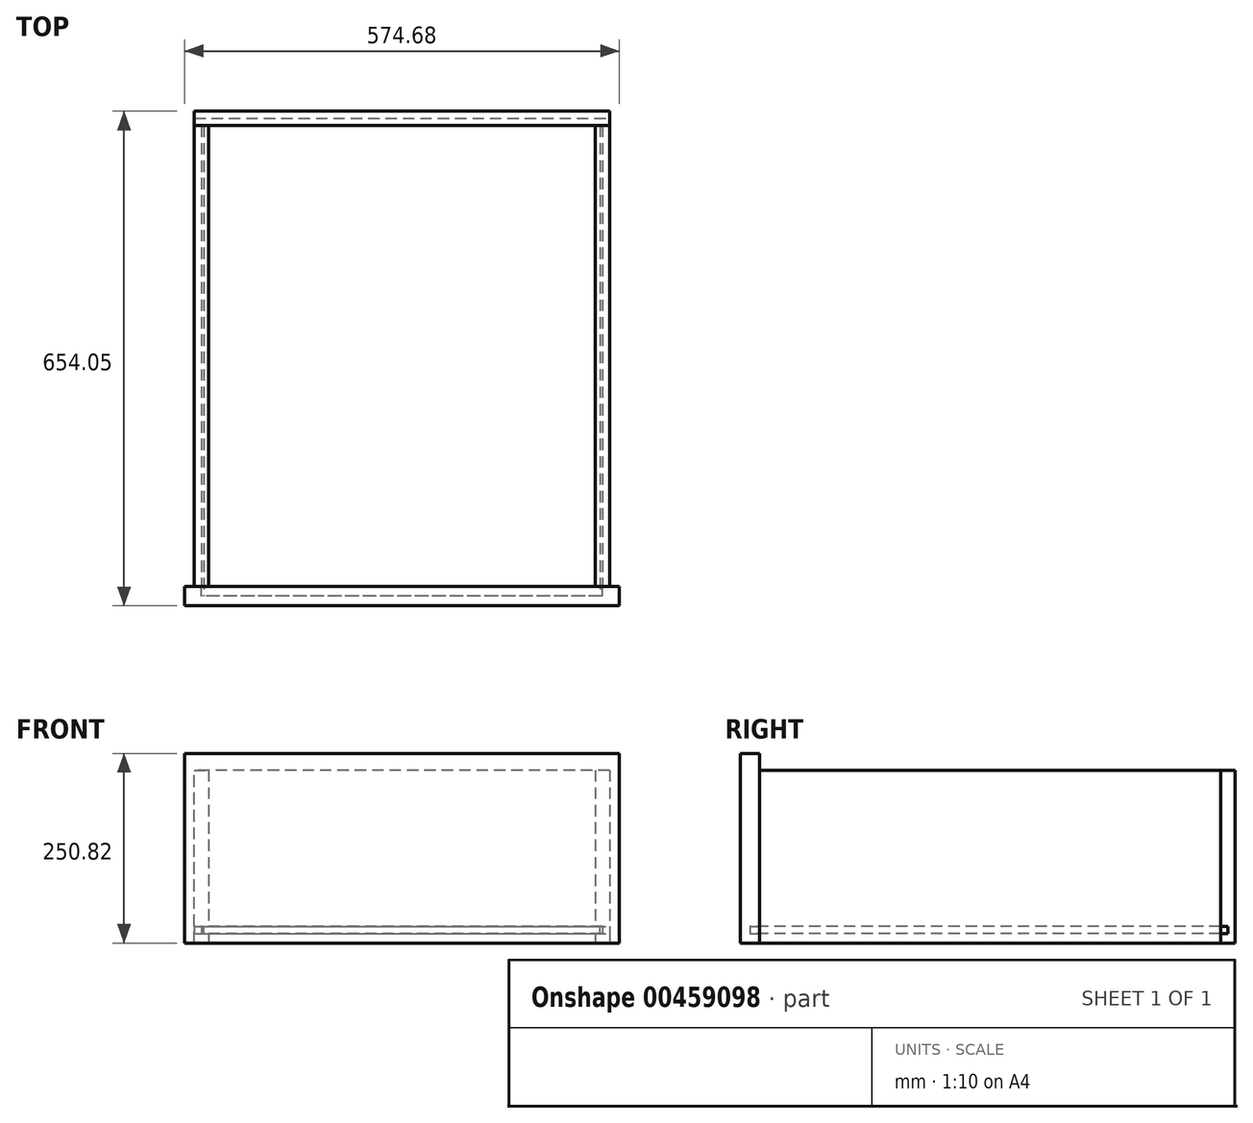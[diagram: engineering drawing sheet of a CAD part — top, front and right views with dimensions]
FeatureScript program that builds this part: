
annotation { "Feature Type Name" : "Feature", "Feature Type Description" : "" }
export const myFeature = defineFeature(function(context is Context, id is Id, definition is map)
    precondition{}
    {
        {
            var Q0;
            Q0=qCreatedBy(makeId("Front.planeOp"),FACE);
            var sketch = newSketch(context, id + "F0", { "sketchPlane" : qUnion([Q0])});
            skLineSegment(sketch, "E0.bottom", {"start": v(-287.34, 125.41) * mm, "end": v(287.34, 125.41) * mm});
            skLineSegment(sketch, "E0.top", {"start": v(-287.34, -125.41) * mm, "end": v(287.34, -125.41) * mm});
            skLineSegment(sketch, "E0.left", {"start": v(-287.34, 125.41) * mm, "end": v(-287.34, -125.41) * mm});
            skLineSegment(sketch, "E0.right", {"start": v(287.34, 125.41) * mm, "end": v(287.34, -125.41) * mm});
            skSolve(sketch);
        }
        {
            var Q0;
            Q0=makeQuery(id+"F0.imprint","IMPRINT",FACE,{"disambiguationData":[TD([[makeQuery(id+"F0.imprint","IMPRINT",EDGE,{"derivedFrom":sQuery(id+"F0.wireOp",EDGE,"E0.bottom")}),-1.0]])]});
            extrude(context, id + "F1", {"entities" : qUnion([Q0]), "depth" : 25.4 * mm});
        }
        {
            var Q0;
            Q0=makeQuery(id+"F1.opExtrude","CAP_FACE",FACE,{"disambiguationData":[OSD([sQuery(id+"F0.wireOp",EDGE,"E0.bottom"),sQuery(id+"F0.wireOp",EDGE,"E0.top"),sQuery(id+"F0.wireOp",EDGE,"E0.left"),sQuery(id+"F0.wireOp",EDGE,"E0.right")])],"isStart":true});
            var sketch = newSketch(context, id + "F2", { "sketchPlane" : qUnion([Q0])});
            skLineSegment(sketch, "E1.bottom", {"start": v(-274.64, 103.19) * mm, "end": v(-255.59, 103.19) * mm});
            skLineSegment(sketch, "E1.top", {"start": v(-274.64, -125.41) * mm, "end": v(-255.59, -125.41) * mm});
            skLineSegment(sketch, "E1.right", {"start": v(-255.59, 103.19) * mm, "end": v(-255.59, -103.19) * mm});
            skLineSegment(sketch, "E2.bottom", {"start": v(274.64, 103.19) * mm, "end": v(255.59, 103.19) * mm});
            skLineSegment(sketch, "E2.top", {"start": v(274.64, -125.41) * mm, "end": v(255.59, -125.41) * mm});
            skLineSegment(sketch, "E2.right", {"start": v(255.59, 103.19) * mm, "end": v(255.59, -103.19) * mm});
            skLineSegment(sketch, "E3.bottom", {"start": v(265.11, -103.19) * mm, "end": v(255.59, -103.19) * mm});
            skLineSegment(sketch, "E3.top", {"start": v(265.11, -112.71) * mm, "end": v(255.59, -112.71) * mm});
            skLineSegment(sketch, "E4", {"start": v(-265.11, -102.9) * mm, "end": v(-265.11, -112.71) * mm});
            skLineSegment(sketch, "E5", {"start": v(265.11, -103.19) * mm, "end": v(265.11, -112.71) * mm});
            skLineSegment(sketch, "E6.trimOffspring", {"start": v(-255.59, -103.19) * mm, "end": v(-265.11, -103.19) * mm});
            skLineSegment(sketch, "E7.trimOffspring", {"start": v(-255.59, -112.71) * mm, "end": v(-265.11, -112.71) * mm});
            skLineSegment(sketch, "E8.trimOffspring", {"start": v(-255.59, -112.71) * mm, "end": v(-255.59, -125.41) * mm});
            skLineSegment(sketch, "E9.trimOffspring", {"start": v(255.59, -112.71) * mm, "end": v(255.59, -125.41) * mm});
            skLineSegment(sketch, "E10", {"start": v(-274.64, 103.19) * mm, "end": v(-274.64, -125.41) * mm});
            skLineSegment(sketch, "E11", {"start": v(274.64, 103.19) * mm, "end": v(274.64, -125.41) * mm});
            skSolve(sketch);
        }
        {
            var Q0;
            Q0 = qSketchRegion(id + "F2", true);
            extrude(context, id + "F3", {"entities" : qUnion([Q0]), "depth" : 609.6 * mm});
        }
        {
            var Q0;
            Q0=makeQuery(id+"F1.opExtrude","CAP_FACE",FACE,{"disambiguationData":[OSD([sQuery(id+"F0.wireOp",EDGE,"E0.bottom"),sQuery(id+"F0.wireOp",EDGE,"E0.top"),sQuery(id+"F0.wireOp",EDGE,"E0.left"),sQuery(id+"F0.wireOp",EDGE,"E0.right")])],"isStart":true});
            var sketch = newSketch(context, id + "F4", { "sketchPlane" : qUnion([Q0])});
            skLineSegment(sketch, "E12.bottom", {"start": v(-265.11, -103.19) * mm, "end": v(265.11, -103.19) * mm});
            skLineSegment(sketch, "E12.top", {"start": v(-265.11, -112.71) * mm, "end": v(265.11, -112.71) * mm});
            skLineSegment(sketch, "E12.left", {"start": v(-265.11, -103.19) * mm, "end": v(-265.11, -112.71) * mm});
            skLineSegment(sketch, "E12.right", {"start": v(265.11, -103.19) * mm, "end": v(265.11, -112.71) * mm});
            skSolve(sketch);
        }
        {
            var Q0;
            Q0 = qSketchRegion(id + "F4", true);
            extrude(context, id + "F5", {"entities" : qUnion([Q0]), "operationType" : NewBodyOperationType.REMOVE, "oppositeDirection" : true, "depth" : 12.7 * mm});
        }
        {
            var Q0;
            Q0=makeQuery(id+"F5.boolean.opBoolean","COPY",FACE,{"derivedFrom":makeQuery(id+"F5.opExtrude","CAP_FACE",FACE,{"disambiguationData":[OSD([sQuery(id+"F4.wireOp",EDGE,"E12.bottom"),sQuery(id+"F4.wireOp",EDGE,"E12.top"),sQuery(id+"F4.wireOp",EDGE,"E12.left"),sQuery(id+"F4.wireOp",EDGE,"E12.right")])],"isStart":false})});
            var sketch = newSketch(context, id + "F6", { "sketchPlane" : qUnion([Q0])});
            skLineSegment(sketch, "E13.bottom", {"start": v(-261.94, -103.19) * mm, "end": v(261.94, -103.19) * mm});
            skLineSegment(sketch, "E13.top", {"start": v(-261.94, -112.71) * mm, "end": v(261.94, -112.71) * mm});
            skLineSegment(sketch, "E13.left", {"start": v(-261.94, -103.19) * mm, "end": v(-261.94, -112.71) * mm});
            skLineSegment(sketch, "E13.right", {"start": v(261.94, -103.19) * mm, "end": v(261.94, -112.71) * mm});
            skSolve(sketch);
        }
        {
            var Q0;
            Q0=makeQuery(id+"F6.imprint","IMPRINT",FACE,{"disambiguationData":[TD([[makeQuery(id+"F6.imprint","IMPRINT",EDGE,{"derivedFrom":sQuery(id+"F6.wireOp",EDGE,"E13.bottom")}),-1.0]])]});
            extrude(context, id + "F7", {"entities" : qUnion([Q0]), "depth" : 628.65 * mm});
        }
        {
            var Q0;
            Q0=makeQuery(id+"F3.opExtrude","CAP_FACE",FACE,{"disambiguationData":[OSD([sQuery(id+"F2.wireOp",EDGE,"E1.bottom"),sQuery(id+"F2.wireOp",EDGE,"E1.top"),sQuery(id+"F2.wireOp",EDGE,"E1.left"),sQuery(id+"F2.wireOp",EDGE,"E1.right"),sQuery(id+"F2.wireOp",EDGE,"E4"),sQuery(id+"F2.wireOp",EDGE,"E6.trimOffspring"),sQuery(id+"F2.wireOp",EDGE,"E7.trimOffspring"),sQuery(id+"F2.wireOp",EDGE,"E8.trimOffspring")])],"isStart":false});
            var sketch = newSketch(context, id + "F8", { "sketchPlane" : qUnion([Q0])});
            skLineSegment(sketch, "E14.bottom", {"start": v(-274.64, -125.41) * mm, "end": v(274.64, -125.41) * mm});
            skLineSegment(sketch, "E14.top", {"start": v(-274.64, 103.19) * mm, "end": v(274.64, 103.19) * mm});
            skLineSegment(sketch, "E14.left", {"start": v(-274.64, -125.41) * mm, "end": v(-274.64, 103.19) * mm});
            skLineSegment(sketch, "E14.right", {"start": v(274.64, -125.41) * mm, "end": v(274.64, 103.19) * mm});
            skSolve(sketch);
        }
        {
            var Q0;
            Q0 = qSketchRegion(id + "F8", true);
            extrude(context, id + "F9", {"entities" : qUnion([Q0]), "depth" : 19.05 * mm});
        }
        {
            var Q0;
            Q0=makeQuery(id+"F9.opExtrude","SWEPT_FACE",FACE,{"disambiguationData":[OSD([sQuery(id+"F8.wireOp",EDGE,"E14.left")])]});
            var sketch = newSketch(context, id + "F10", { "sketchPlane" : qUnion([Q0])});
            skLineSegment(sketch, "E15.bottom", {"start": v(609.6, -103.19) * mm, "end": v(619.12, -103.19) * mm});
            skLineSegment(sketch, "E15.top", {"start": v(609.6, -112.71) * mm, "end": v(619.12, -112.71) * mm});
            skLineSegment(sketch, "E15.left", {"start": v(609.6, -103.19) * mm, "end": v(609.6, -112.71) * mm});
            skLineSegment(sketch, "E15.right", {"start": v(619.12, -103.19) * mm, "end": v(619.12, -112.71) * mm});
            skSolve(sketch);
        }
        {
            var Q0;
            Q0 = qSketchRegion(id + "F10", true);
            extrude(context, id + "F11", {"entities" : qUnion([Q0]), "operationType" : NewBodyOperationType.REMOVE, "oppositeDirection" : true, "depth" : 584.2 * mm});
        }
    });
